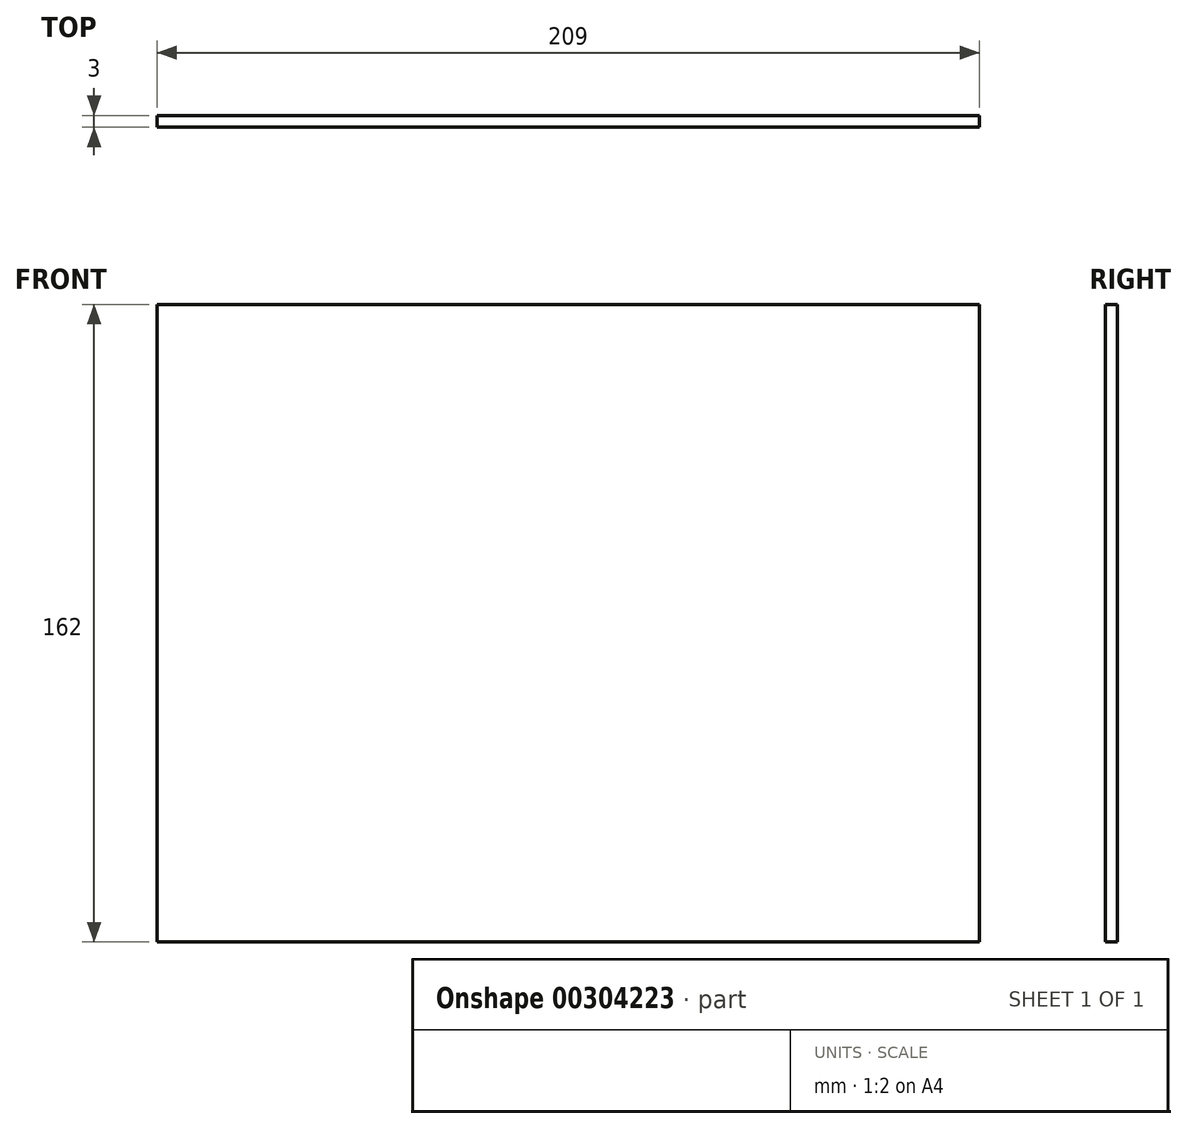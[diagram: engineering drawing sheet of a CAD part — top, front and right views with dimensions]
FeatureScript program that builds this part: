
annotation { "Feature Type Name" : "Feature", "Feature Type Description" : "" }
export const myFeature = defineFeature(function(context is Context, id is Id, definition is map)
    precondition{}
    {
        {
            var Q0;
            Q0=qCreatedBy(makeId("Front.planeOp"),FACE);
            var sketch = newSketch(context, id + "F0", { "sketchPlane" : qUnion([Q0])});
            skLineSegment(sketch, "E0.bottom", {"start": v(0, 0) * mm, "end": v(209, 0) * mm});
            skLineSegment(sketch, "E0.top", {"start": v(0, 162) * mm, "end": v(209, 162) * mm});
            skLineSegment(sketch, "E0.left", {"start": v(0, 0) * mm, "end": v(0, 162) * mm});
            skLineSegment(sketch, "E0.right", {"start": v(209, 0) * mm, "end": v(209, 162) * mm});
            skSolve(sketch);
        }
        {
            var Q0;
            Q0=makeQuery(id+"F0.imprint","IMPRINT",FACE,{"disambiguationData":[TD([[makeQuery(id+"F0.imprint","IMPRINT",EDGE,{"derivedFrom":sQuery(id+"F0.wireOp",EDGE,"E0.bottom")}),1.0]])]});
            extrude(context, id + "F1", {"entities" : qUnion([Q0]), "depth" : 3 * mm});
        }
    });
